FCSTD DOCUMENT  (FreeCAD 0.19R24276 (Git))
Label: pir-baffel-screwBlock-assembly
License: All rights reserved
LicenseURL: http://en.wikipedia.org/wiki/All_rights_reserved
objects: App::Link×3, App::DocumentObjectGroup×2, PartDesign::CoordinateSystem×1, App::FeaturePython×1, App::Part×1
note: 1 computed .brp shape members not serialized (recipe doc carries the construction recipe); baked Part::Feature solids carry a one-line shape summary decoded from their .brp
EXTERNAL_REF file=pir-baffel-screw-blocks.FCStd obj=LCS_screwBlock
EXTERNAL_REF file=pir-baffel-screw-blocks.FCStd obj=Body

FEATURE [App::DocumentObjectGroup] Parts
FEATURE [PartDesign::CoordinateSystem] LCS_Origin
  AttacherType = Attacher::AttachEngine3D
  MapMode = 2
  Support = -> [X_Axis]
FEATURE [App::DocumentObjectGroup] Constraints
FEATURE [App::FeaturePython] Variables  # WARN: FeaturePython — macro-defined, semantics opaque (R4)
FEATURE [App::Link] pir_baffel_screw_blocks_Body  label="pir_baffel_screw_block1_Body"
  AssemblyType = Asm4EE
  AttachedBy = #LCS_screwBlock
  AttachedTo = Parent Assembly#LCS_Origin
  LinkPlacement = pos=(-1e-16,2e-16,-1.6) rot=(0,0,-1;1.5708rad)
  LinkedObject = -> <external pir-baffel-screw-blocks.FCStd>#Body
  Placement = pos=(-1e-16,2e-16,-1.6) rot=(0,0,-1;1.5708rad)
  expr: Placement = LCS_Origin.Placement * AttachmentOffset * pir_baffel_screw_blocks#LCS_screwBlock.Placement ^ -1
FEATURE [App::Link] pir_baffel_screw_block2_Body
  AssemblyType = Asm4EE
  AttachedBy = #LCS_screwBlock
  AttachedTo = pir_baffel_screw_blocks_Body#LCS_screwBlock
  AttachmentOffset = pos=(0,0,1.6) rot=(0,0,1;0rad)
  LinkPlacement = pos=(-1e-16,2e-16,0) rot=(0,0,-1;1.5708rad)
  LinkedObject = -> <external pir-baffel-screw-blocks.FCStd>#Body
  Placement = pos=(-1e-16,2e-16,0) rot=(0,0,-1;1.5708rad)
  expr: Placement = pir_baffel_screw_blocks_Body.Placement * pir_baffel_screw_blocks#LCS_screwBlock.Placement * AttachmentOffset * pir_baffel_screw_blocks#LCS_screwBlock.Placement ^ -1
FEATURE [App::Link] pir_baffel_screw_block3_Body
  AssemblyType = Asm4EE
  AttachedBy = #LCS_screwBlock
  AttachedTo = pir_baffel_screw_block2_Body#LCS_screwBlock
  AttachmentOffset = pos=(0,0,1.6) rot=(0,0,1;0rad)
  LinkPlacement = pos=(-1e-16,2e-16,1.6) rot=(0,0,-1;1.5708rad)
  LinkedObject = -> <external pir-baffel-screw-blocks.FCStd>#Body
  Placement = pos=(-1e-16,2e-16,1.6) rot=(0,0,-1;1.5708rad)
  expr: Placement = pir_baffel_screw_block2_Body.Placement * pir_baffel_screw_blocks#LCS_screwBlock.Placement * AttachmentOffset * pir_baffel_screw_blocks#LCS_screwBlock.Placement ^ -1
FEATURE [App::Part] Model
  Configuration = 0
  Group = -> [LCS_Origin,Constraints,Variables,pir_baffel_screw_blocks_Body,pir_baffel_screw_block2_Body,pir_baffel_screw_block3_Body]
  Origin = -> Origin
  Type = Assembly4 Model

RESOLVED EXTERNAL PARTS (link-assembly join: the EXTERNAL_REF files above that resolve inside this repo's crawl, each included once):
---- part pir-baffel-screw-blocks.FCStd = doc fcstd_95a1c698f783 ----
FCSTD DOCUMENT  (FreeCAD 0.19R24276 (Git))
Label: pir-baffel-screw-blocks
License: All rights reserved
LicenseURL: http://en.wikipedia.org/wiki/All_rights_reserved
objects: Sketcher::SketchObject×1, PartDesign::Pad×1, PartDesign::CoordinateSystem×1, PartDesign::Body×1
note: 5 computed .brp shape members not serialized (recipe doc carries the construction recipe); baked Part::Feature solids carry a one-line shape summary decoded from their .brp

FEATURE [Sketcher::SketchObject] Sketch
  FullyConstrained = true
  MapMode = 5
  Support = -> [XY_Plane]
  sketch-geometry (4):
    g0: LineSegment StartX=-15 StartY=7.5 StartZ=0 EndX=15 EndY=7.5 EndZ=0
    g1: LineSegment StartX=15 StartY=7.5 StartZ=0 EndX=15 EndY=-7.5 EndZ=0
    g2: LineSegment StartX=15 StartY=-7.5 StartZ=0 EndX=-15 EndY=-7.5 EndZ=0
    g3: LineSegment StartX=-15 StartY=-7.5 StartZ=0 EndX=-15 EndY=7.5 EndZ=0
  constraints (10):
    c: Coincident(g0,g1)
    c: Coincident(g1,g2)
    c: Coincident(g2,g3)
    c: Coincident(g3,g0)
    c: Horizontal(g2)
    c: Vertical(g1)
    c: DistanceX(g0,g0) = 30
    c: DistanceY(g3,g3) = 15
    c: Symmetric(g0,g2,g-1)
    c: Symmetric(g0,g0,g-2)
FEATURE [PartDesign::Pad] Pad  label="ScrewBlock"
  Direction = (1,1,1)
  Length = 1.6
  Length2 = 100
  Profile = -> Sketch
  Type = 0
FEATURE [PartDesign::CoordinateSystem] LCS_screwBlock
  AttacherType = Attacher::AttachEngine3D
  MapMode = 45
  Placement = pos=(2e-16,1e-16,1.6) rot=(0,0,1;1.5708rad)
  Support = -> [Pad]
FEATURE [PartDesign::Body] Body
  Group = -> [Sketch,Pad,LCS_screwBlock]
  Origin = -> Origin
  Tip = -> Pad
